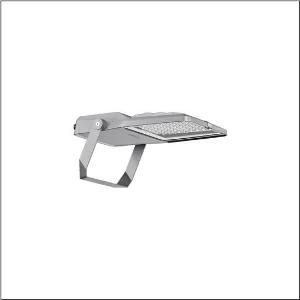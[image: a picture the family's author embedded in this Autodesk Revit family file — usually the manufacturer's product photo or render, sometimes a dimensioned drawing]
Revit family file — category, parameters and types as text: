
# Revit family: floodlight_fl_21_iq_mini___pl43_5xa7772b5a1a_c178
name_source: partatom
category: Lighting Fixtures
units: mm (PartAtom-declared; Revit-internal decimal feet)

## family parameters
Cut with Voids When Loaded = No
Host = Face
Light Source = No
Part Type = Normal
Room Calculation Point = No
Round Connector Dimension = Use Diameter
Shared = No

## types (1)
- --- (1 x LED, 5970 lm, 45.5 W, 4000K)
    Apparent Load = 46 VA
    CIE Flux Codes = 27 78 99 100 100
    Color Rendering = 80
    Color Temperature = 4000K
    Default Elevation = 1800 mm
    Description = Floodlight FL 21 iQ mini, floodlight, primary light control with lens, of PMMA, primary optical cover: protective disc, of toughened safety glass, transparent, light distribution: PL43, light emission: direct distribution, installation type: surface-mounted, lamps: LED, High Power LED, rated values: 5.970lm | 45,5W | 131,2lm/W (begin service life); end service life: 5.970lm | 48W; at 50% lumin. flux: 2.985lm | 21,5W | 138,8lm/W, colour temperature: 4000K, colour rendering: CRI > 80, light colour: 840, light setting 1 begin service life: 100% | 5.970lm | 45,5W | 131,2lm/W | 4.000K, light setting 1 end service life: 48W, further light settings possible, control: Street-Remote, Auto-Match, Temp-Guard, Night-Set, Smart-Wire, Desk-Remote (wireless, voltage-free reading and setting of iQ features in the workshop via application-optimized NFC function/RFID function), optimised constant luminous flux control (CLO 2.0), pre-setting: linear dimming characteristic, with terminal, 6-pole, mains connection: 220..240V, AC, 50/60Hz, luminaire housing, of diecast aluminium, powder-coated, SITECO metallic grey (DB 702S), corrosivity category C5 mid according to DIN EN ISO 12944suitable for swimming poolschlorine-resistant, sealing non-destructively replaceable, mounting bracket, of steel, galvanised, powder-coated, SITECO metallic grey (DB 702S), protection rating (complete): IP66, insulation class (complete): insulation class II (safety insulation), certification: CE, ENEC, VDE, protection symbol: D, impact resistance: IK08, permissible operating ambient temperature: -40..+40°C, permissible operating ambient temperature for outdoor applications: -40..+50°C, standard: DIN EN 12944, LABS conformity tested according to VDMA 24364:2018-05, packaging unit: 1 piece

Light Distribution: PL43
    Height = 70 mm
    Lamp = 1 x LED
    Lamp Light Flux = 5970 lm
    Lamp Power = 45.5 W
    Lamp count = 1
    Length = 485 mm
    Luminous efficacy = 131 lm/W
    Manufacturer = Siteco
    ModVariant = No
    Model = 5XA7772B5A1A
    Mounting Place = Pole
    Mounting Type = Pole annexe
    Number of Poles = 1
    OnlyDefault = Yes
    Power Factor = 1
    Product Name = Floodlight FL 21 iQ mini | PL43
    Product group = floodlight | pylon annexe
    ProductGroupID = 6201
    Protection Class = Protection class II
    Protection Degree = IP 66
    RLX_Detail_Level = 1
    RLX_Emergency_Light_Flux = 0 lm
    RLX_Emergency_Type = 0
    RLX_Emergency_Type_DB = No
    RlxData = <blob elided: 96393 chars, md5=74686ded>
    Socket = socket
    Standby Power = 0 W
    System Light Flux = 5970 lm
    System Power = 46 W
    Type Comments = factory setting: luminous flux: 100 % | dim-lin: 254 | 463 mA
    Type Image = l_1006845.jpg
    URL = http://relux.com
    VarID = @adj_163663
    Voltage = 0 V
    Weight = 0.00 kg
    Width = 337 mm

## geometry (parser evidence)
native form markers: Blend x4, Sweep x12
no freeform markers — native parametric forms only
